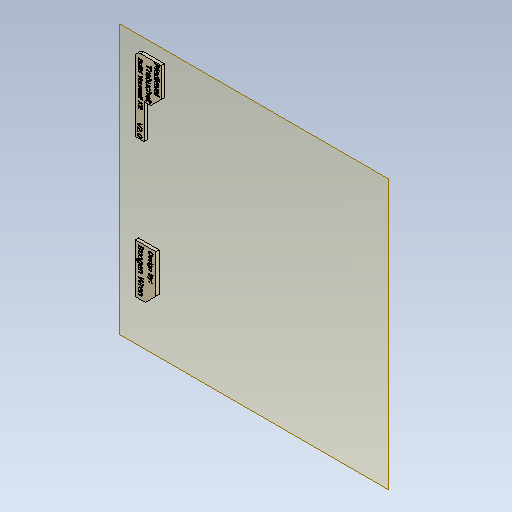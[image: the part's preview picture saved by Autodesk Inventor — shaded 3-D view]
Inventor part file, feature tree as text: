
AUTODESK INVENTOR PART (.ipt)
format: ipt  version: 2023 (Build 270158030, 158C)  size: 1,380,864 bytes
history: native  units: mm
features: other x3, plane x2, sketch x2, extrude x2, chamfer x1, reference x1
ambient origin geometry x8: Origin, YZ Plane, XZ Plane, XY Plane, X Axis, Y Axis, Z Axis, Center Point
bodies: Solid1 (feature_tree)
feature tree (11):
  plane  "Work Plane1"
  sketch  "Sketch1"  dims[d0=19.431275mm d1=23.65936mm]
  plane  "Work Plane2"
  extrude  "Extrusion1"  Depth=23.65936mm
  sketch  "Sketch2"  dims[d2=67.883459mm d3=8.354057mm d4=46.297087mm d5=37.541436mm d6=24.543837mm d7=70.0mm d8=10.0mm d9=0.0mm d10=10.0mm d11=2.0mm d12=45.0deg d19=2.0mm d20=0.0mm]
  chamfer  "Chamfer1"  Distance=8.354057mm
  extrude  "Extrusion2"  Depth=46.297087mm
  reference  "Reference1"
  other  "<userpath>\Documents\0004-inventor\3D-CAD-main\trebuchet\V4.0-trebuchet-printable.iam"
  other  "V4.0-trebuchet-printable.iam"
  other  "border:1"
